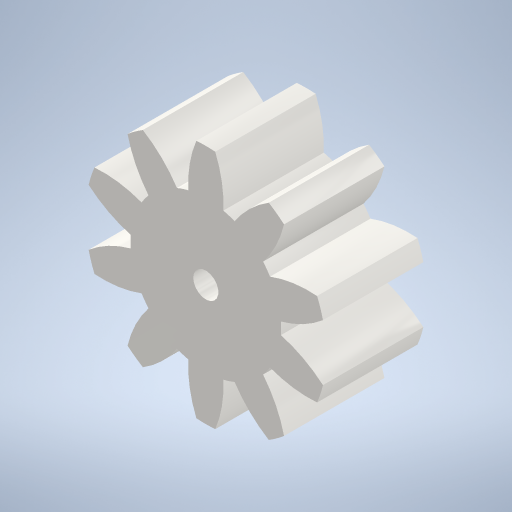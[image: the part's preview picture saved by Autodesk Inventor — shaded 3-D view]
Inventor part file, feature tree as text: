
AUTODESK INVENTOR PART (.ipt)
format: ipt  version: 2024 (Build 280153000, 153)  size: 314,368 bytes
history: native  units: mm (DEFAULTED — no unit token found)
features: plane x3, other x3, extrude x2, sketch x2
ambient origin geometry x8: Origin, YZ Plane, XZ Plane, XY Plane, X Axis, Y Axis, Z Axis, Center Point
bodies: Solid1 (feature_tree)
feature tree (10):
  extrude  "Extrusion1"  Depth=10.0mm TaperAngle=0.0deg
  plane  "Work Plane2"
  plane  "Work Plane8"
  plane  "Work Plane9"
  other  "Spur Gear"
  extrude  "Extrusion2"  Depth=10.0mm TaperAngle=0.0deg
  sketch  "Sketch1"  dims[d0=24.0mm d1=10.0mm d2=0.0mm]
  other  "Srf1"
  sketch  "Sketch3"  dims[d3=20.0mm d4=10.0mm d5=0.0mm d16=40.0mm d17=0.0mm d34=3.141593mm d39=0.0mm d41=0.0mm d43=40.0mm d46=40.0mm d47=0.0mm d48=0.0mm d49=2.5mm d50=10.0mm d51=0.0mm d52=0.5mm d53=0.872665mm]
  other  "Pitch Diameter"
